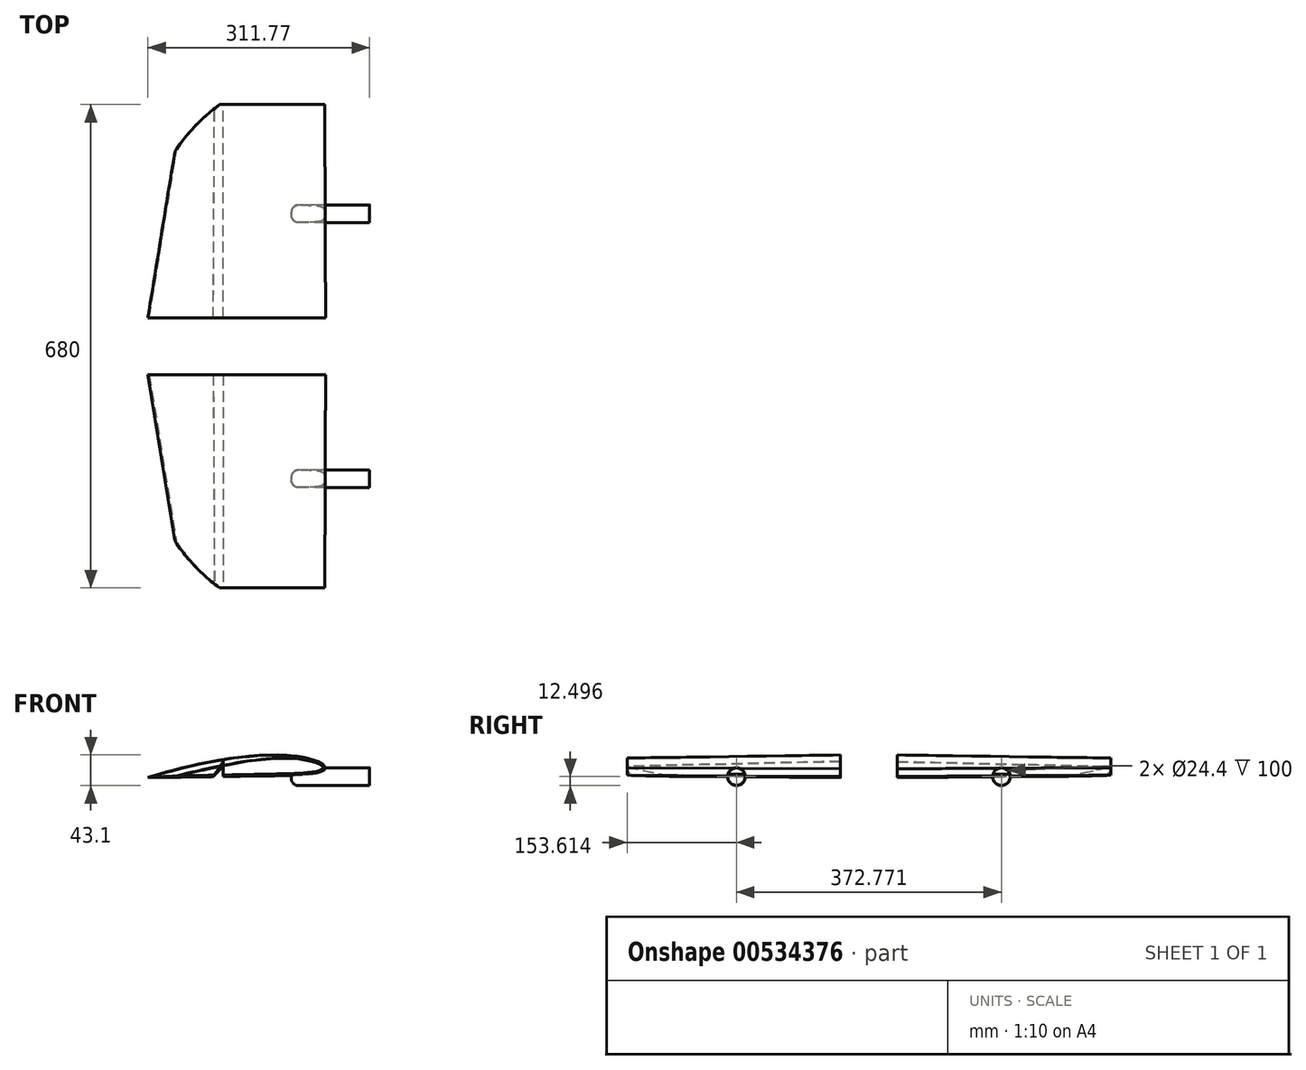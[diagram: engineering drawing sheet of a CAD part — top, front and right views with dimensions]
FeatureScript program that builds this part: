
annotation { "Feature Type Name" : "Feature", "Feature Type Description" : "" }
export const myFeature = defineFeature(function(context is Context, id is Id, definition is map)
    precondition{}
    {
        {
            var Q0;
            Q0=qCreatedBy(makeId("Front.planeOp"),FACE);
            var sketch = newSketch(context, id + "F0", { "sketchPlane" : qUnion([Q0])});
            skFitSpline(sketch, "E0.0.0", {"points": [v(128.23, 37.15) * mm, v(128.28, 37.44) * mm, v(128.28, 38.04) * mm, v(128.05, 38.94) * mm, v(127.62, 39.8) * mm, v(127.03, 40.64) * mm, v(126.33, 41.42) * mm, v(125.54, 42.16) * mm, v(124.7, 42.86) * mm, v(123.52, 43.74) * mm, v(121.98, 44.75) * mm, v(120.1, 45.83) * mm, v(118.53, 46.62) * mm, v(117.3, 47.2) * mm, v(116.38, 47.59) * mm, v(115.47, 47.96) * mm, v(114.57, 48.31) * mm, v(113.66, 48.64) * mm, v(112.75, 48.96) * mm, v(111.84, 49.27) * mm, v(110.6, 49.67) * mm, v(109, 50.17) * mm, v(107.06, 50.76) * mm, v(105.09, 51.33) * mm, v(103.1, 51.88) * mm, v(101.1, 52.4) * mm, v(99.12, 52.87) * mm, v(97.15, 53.31) * mm, v(95.18, 53.71) * mm, v(93.2, 54.08) * mm, v(91.23, 54.41) * mm, v(88.57, 54.83) * mm, v(85.22, 55.28) * mm, v(81.18, 55.73) * mm, v(77.14, 56.06) * mm, v(73.1, 56.3) * mm, v(69.07, 56.46) * mm, v(65.02, 56.57) * mm, v(59.62, 56.64) * mm, v(54.22, 56.62) * mm, v(48.82, 56.5) * mm, v(44.78, 56.38) * mm, v(40.73, 56.22) * mm, v(36.7, 56.02) * mm, v(32.65, 55.78) * mm, v(27.27, 55.4) * mm, v(20.55, 54.85) * mm, v(13.83, 54.19) * mm, v(8.47, 53.59) * mm, v(4.45, 53.1) * mm, v(0.43, 52.59) * mm, v(-4.92, 51.86) * mm, v(-11.6, 50.88) * mm, v(-18.25, 49.8) * mm, v(-23.57, 48.9) * mm, v(-27.55, 48.18) * mm, v(-31.53, 47.44) * mm, v(-36.82, 46.43) * mm, v(-43.4, 45.1) * mm, v(-49.97, 43.7) * mm, v(-55.24, 42.54) * mm, v(-59.19, 41.65) * mm, v(-63.13, 40.73) * mm, v(-67.06, 39.8) * mm, v(-70.98, 38.86) * mm, v(-74.25, 38.05) * mm, v(-76.87, 37.4) * mm, v(-79.49, 36.74) * mm, v(-84.07, 35.57) * mm, v(-88.66, 34.37) * mm, v(-92.57, 33.32) * mm, v(-94.53, 32.8) * mm, v(-96.48, 32.26) * mm, v(-98.44, 31.73) * mm, v(-100.42, 31.18) * mm, v(-102.4, 30.63) * mm, v(-104.36, 30.08) * mm, v(-106.3, 29.53) * mm, v(-108.25, 28.97) * mm, v(-110.2, 28.41) * mm, v(-112.13, 27.84) * mm, v(-114.7, 27.08) * mm, v(-117.91, 26.1) * mm, v(-120.48, 25.29) * mm, v(-121.77, 24.87) * mm]});
            skFitSpline(sketch, "E0.0.1", {"points": [v(-121.77, 24.87) * mm, v(-120.44, 24.86) * mm, v(-117.77, 24.85) * mm, v(-113.77, 24.85) * mm, v(-109.82, 24.88) * mm, v(-105.88, 24.93) * mm, v(-101.92, 24.98) * mm, v(-97.92, 25.04) * mm, v(-93.93, 25.1) * mm, v(-89.93, 25.16) * mm, v(-86.6, 25.21) * mm, v(-83.93, 25.25) * mm, v(-81.93, 25.28) * mm, v(-79.94, 25.31) * mm, v(-77.97, 25.34) * mm, v(-76.05, 25.37) * mm, v(-74.17, 25.4) * mm, v(-72.34, 25.43) * mm, v(-69.94, 25.46) * mm, v(-67.55, 25.5) * mm, v(-65.12, 25.54) * mm, v(-63.26, 25.56) * mm, v(-61.35, 25.6) * mm, v(-59.4, 25.62) * mm, v(-57.74, 25.64) * mm, v(-56.4, 25.66) * mm, v(-55.07, 25.68) * mm, v(-53.4, 25.7) * mm, v(-50.74, 25.74) * mm, v(-47.41, 25.8) * mm, v(-43.41, 25.85) * mm, v(-40.08, 25.9) * mm, v(-37.42, 25.94) * mm, v(-35.42, 25.97) * mm, v(-33.42, 26) * mm, v(-31.42, 26.02) * mm, v(-29.42, 26.05) * mm, v(-27.47, 26.08) * mm, v(-25.57, 26.1) * mm, v(-23.73, 26.14) * mm, v(-21.95, 26.16) * mm, v(-19.62, 26.2) * mm, v(-17.32, 26.23) * mm, v(-14.96, 26.27) * mm, v(-13.15, 26.3) * mm, v(-11.27, 26.32) * mm, v(-9.34, 26.35) * mm, v(-7.69, 26.37) * mm, v(-6.35, 26.39) * mm, v(-5.02, 26.4) * mm, v(-3.36, 26.43) * mm, v(-0.7, 26.47) * mm, v(2.64, 26.52) * mm, v(6.64, 26.58) * mm, v(11.97, 26.66) * mm, v(18.63, 26.75) * mm, v(26.63, 26.86) * mm, v(34.62, 26.98) * mm, v(42.62, 27.1) * mm, v(50.61, 27.2) * mm, v(57.27, 27.3) * mm, v(62.6, 27.39) * mm, v(66.6, 27.46) * mm, v(70.6, 27.53) * mm, v(74.59, 27.62) * mm, v(77.9, 27.7) * mm, v(80.57, 27.79) * mm, v(82.58, 27.86) * mm, v(84.58, 27.93) * mm, v(86.59, 28.01) * mm, v(88.58, 28.1) * mm, v(90.57, 28.18) * mm, v(92.55, 28.27) * mm, v(94.53, 28.37) * mm, v(96.52, 28.5) * mm, v(98.52, 28.63) * mm, v(100.54, 28.8) * mm, v(102.56, 28.98) * mm, v(104.59, 29.17) * mm, v(106.6, 29.37) * mm, v(108.57, 29.57) * mm, v(110.5, 29.75) * mm, v(112.4, 29.94) * mm, v(114.3, 30.16) * mm, v(115.92, 30.41) * mm, v(117.24, 30.67) * mm, v(118.58, 30.97) * mm, v(120.29, 31.43) * mm, v(122.33, 32.13) * mm, v(123.99, 32.86) * mm, v(125.23, 33.55) * mm, v(126.1, 34.13) * mm, v(126.88, 34.78) * mm, v(127.53, 35.5) * mm, v(128.01, 36.3) * mm, v(128.19, 36.86) * mm, v(128.23, 37.15) * mm]});
            skLineSegment(sketch, "E1", {"start": v(-15.83, 26.25) * mm, "end": v(-15.83, 46.77) * mm});
            skLineSegment(sketch, "E2", {"start": v(-15.83, 46.77) * mm, "end": v(-29.65, 26.05) * mm});
            skSolve(sketch);
        }
        {
            var Q0;
            Q0=qCreatedBy(makeId("Front.planeOp"),FACE);
            cPlane(context, id + "F1", {"entities" : qUnion([Q0]), "cplaneType" : CPlaneType.OFFSET, "offset" : 300 * mm, "width" : 150 * mm, "height" : 150 * mm});
        }
        {
            var Q0;
            Q0=qCreatedBy(id+"F1.planeOp",FACE);
            var sketch = newSketch(context, id + "F2", { "sketchPlane" : qUnion([Q0])});
            skFitSpline(sketch, "E3.0.0", {"points": [v(127.87, 35.85) * mm, v(127.9, 36.15) * mm, v(127.88, 36.74) * mm, v(127.6, 37.63) * mm, v(127.12, 38.48) * mm, v(126.5, 39.28) * mm, v(125.75, 40.03) * mm, v(124.93, 40.73) * mm, v(124.05, 41.38) * mm, v(122.83, 42.2) * mm, v(121.24, 43.13) * mm, v(119.3, 44.12) * mm, v(117.7, 44.83) * mm, v(116.43, 45.34) * mm, v(115.5, 45.69) * mm, v(114.57, 46.01) * mm, v(113.65, 46.32) * mm, v(112.73, 46.6) * mm, v(111.8, 46.88) * mm, v(110.87, 47.14) * mm, v(109.6, 47.48) * mm, v(108, 47.9) * mm, v(106.02, 48.39) * mm, v(104.02, 48.86) * mm, v(102, 49.3) * mm, v(99.99, 49.72) * mm, v(97.98, 50.1) * mm, v(95.99, 50.44) * mm, v(94, 50.74) * mm, v(92, 51) * mm, v(90, 51.24) * mm, v(87.33, 51.52) * mm, v(83.96, 51.8) * mm, v(79.9, 52.05) * mm, v(75.85, 52.18) * mm, v(71.8, 52.21) * mm, v(67.75, 52.17) * mm, v(63.7, 52.07) * mm, v(58.3, 51.87) * mm, v(52.9, 51.57) * mm, v(47.52, 51.2) * mm, v(43.48, 50.87) * mm, v(39.44, 50.5) * mm, v(35.41, 50.1) * mm, v(31.39, 49.65) * mm, v(26.02, 49) * mm, v(19.33, 48.11) * mm, v(12.66, 47.1) * mm, v(7.32, 46.24) * mm, v(3.33, 45.55) * mm, v(-0.66, 44.84) * mm, v(-5.97, 43.84) * mm, v(-12.6, 42.52) * mm, v(-19.2, 41.11) * mm, v(-24.46, 39.93) * mm, v(-28.41, 39.02) * mm, v(-32.35, 38.08) * mm, v(-37.59, 36.8) * mm, v(-44.1, 35.14) * mm, v(-50.6, 33.41) * mm, v(-55.8, 31.98) * mm, v(-59.7, 30.9) * mm, v(-63.6, 29.78) * mm, v(-67.48, 28.65) * mm, v(-71.35, 27.5) * mm, v(-74.58, 26.54) * mm, v(-77.17, 25.75) * mm, v(-79.75, 24.96) * mm, v(-84.27, 23.56) * mm, v(-88.8, 22.13) * mm, v(-92.66, 20.89) * mm, v(-94.58, 20.26) * mm, v(-96.5, 19.63) * mm, v(-98.45, 19) * mm, v(-100.4, 18.35) * mm, v(-102.34, 17.7) * mm, v(-104.27, 17.05) * mm, v(-106.2, 16.4) * mm, v(-108.11, 15.75) * mm, v(-110.03, 15.09) * mm, v(-111.93, 14.42) * mm, v(-114.46, 13.53) * mm, v(-117.62, 12.38) * mm, v(-120.15, 11.44) * mm, v(-121.42, 10.97) * mm]});
            skFitSpline(sketch, "E3.0.1", {"points": [v(-122.73, 26.21) * mm, v(-121.4, 26.2) * mm, v(-118.72, 26.2) * mm, v(-114.72, 26.23) * mm, v(-110.76, 26.28) * mm, v(-106.83, 26.34) * mm, v(-102.86, 26.42) * mm, v(-98.86, 26.5) * mm, v(-94.86, 26.58) * mm, v(-90.86, 26.66) * mm, v(-87.53, 26.72) * mm, v(-84.86, 26.78) * mm, v(-82.86, 26.82) * mm, v(-80.86, 26.86) * mm, v(-78.9, 26.9) * mm, v(-76.97, 26.94) * mm, v(-75.1, 26.98) * mm, v(-73.26, 27.01) * mm, v(-70.85, 27.06) * mm, v(-68.47, 27.1) * mm, v(-66.03, 27.16) * mm, v(-64.17, 27.2) * mm, v(-62.26, 27.23) * mm, v(-60.3, 27.27) * mm, v(-58.64, 27.3) * mm, v(-57.3, 27.33) * mm, v(-55.98, 27.35) * mm, v(-54.3, 27.38) * mm, v(-51.64, 27.44) * mm, v(-48.3, 27.5) * mm, v(-44.3, 27.58) * mm, v(-40.97, 27.64) * mm, v(-38.3, 27.7) * mm, v(-36.3, 27.73) * mm, v(-34.3, 27.77) * mm, v(-32.3, 27.81) * mm, v(-30.3, 27.85) * mm, v(-28.35, 27.89) * mm, v(-26.45, 27.93) * mm, v(-24.6, 27.96) * mm, v(-22.82, 28) * mm, v(-20.49, 28.04) * mm, v(-18.19, 28.09) * mm, v(-15.83, 28.13) * mm, v(-14.01, 28.17) * mm, v(-12.14, 28.2) * mm, v(-10.2, 28.24) * mm, v(-8.55, 28.28) * mm, v(-7.22, 28.3) * mm, v(-5.88, 28.33) * mm, v(-4.22, 28.36) * mm, v(-1.55, 28.41) * mm, v(1.78, 28.48) * mm, v(5.79, 28.55) * mm, v(11.12, 28.66) * mm, v(17.79, 28.79) * mm, v(25.79, 28.94) * mm, v(33.79, 29.1) * mm, v(41.8, 29.25) * mm, v(49.8, 29.4) * mm, v(56.46, 29.53) * mm, v(61.8, 29.64) * mm, v(65.8, 29.73) * mm, v(69.8, 29.83) * mm, v(73.79, 29.93) * mm, v(77.1, 30.03) * mm, v(79.78, 30.13) * mm, v(81.78, 30.21) * mm, v(83.8, 30.3) * mm, v(85.8, 30.39) * mm, v(87.8, 30.48) * mm, v(89.79, 30.58) * mm, v(91.77, 30.68) * mm, v(93.75, 30.79) * mm, v(95.74, 30.91) * mm, v(97.74, 31.06) * mm, v(99.76, 31.24) * mm, v(101.78, 31.43) * mm, v(103.8, 31.64) * mm, v(105.81, 31.85) * mm, v(107.79, 32.05) * mm, v(109.72, 32.25) * mm, v(111.63, 32.44) * mm, v(113.53, 32.68) * mm, v(115.15, 32.94) * mm, v(116.47, 33.2) * mm, v(117.8, 33.5) * mm, v(119.51, 33.97) * mm, v(121.56, 34.69) * mm, v(123.2, 35.43) * mm, v(124.45, 36.12) * mm, v(125.31, 36.7) * mm, v(126.1, 37.36) * mm, v(126.74, 38.08) * mm, v(127.22, 38.88) * mm, v(127.39, 39.45) * mm, v(127.43, 39.74) * mm]});
            skLineSegment(sketch, "E4", {"start": v(-15.82, 28.13) * mm, "end": v(-15.82, 40.03) * mm});
            skLineSegment(sketch, "E5", {"start": v(-15.82, 40.03) * mm, "end": v(-28.06, 27.9) * mm});
            skSolve(sketch);
        }
        {
            var Q0;
            Q0=makeQuery(id+"F0.imprint","IMPRINT",FACE,{"disambiguationData":[TD([[makeQuery(id+"F0.imprint","IMPRINT",EDGE,{"derivedFrom":sQuery(id+"F0.wireOp",EDGE,"E0.0.0")}),1.0]])]});
            var Q1;
            Q1=makeQuery(id+"F2.imprint","IMPRINT",FACE,{"disambiguationData":[TD([[makeQuery(id+"F2.imprint","IMPRINT",EDGE,{"derivedFrom":sQuery(id+"F2.wireOp",EDGE,"E3.0.0")}),1.0]])]});
            loft(context, id + "F3", {"sheetProfilesArray" : [{ "sheetProfileEntities" : qUnion([Q0]) }, { "sheetProfileEntities" : qUnion([Q1]) }]});
        }
        {
            var Q0;
            Q0=qCreatedBy(makeId("Front.planeOp"),FACE);
            cPlane(context, id + "F4", {"entities" : qUnion([Q0]), "cplaneType" : CPlaneType.OFFSET, "offset" : 40 * mm, "oppositeDirection" : true, "width" : 150 * mm, "height" : 150 * mm});
        }
        {
            var Q0;
            Q0=makeQuery(id+"F3.opLoft","SWEPT_BODY",BODY,{"disambiguationData":[OSD([makeQuery(id+"F0.imprint","IMPRINT",FACE,{"disambiguationData":[TD([[makeQuery(id+"F0.imprint","IMPRINT",EDGE,{"derivedFrom":sQuery(id+"F0.wireOp",EDGE,"E0.0.0")}),1.0]])]}),makeQuery(id+"F2.imprint","IMPRINT",FACE,{"disambiguationData":[TD([[makeQuery(id+"F2.imprint","IMPRINT",EDGE,{"derivedFrom":sQuery(id+"F2.wireOp",EDGE,"E3.0.0")}),1.0]])]})])]});
            var Q1;
            Q1=qCreatedBy(id+"F4.planeOp",FACE);
            mirror(context, id + "F5", {"entities" : qUnion([Q0]), "mirrorPlane" : qUnion([Q1])});
        }
        {
            var Q0;
            Q0=qCreatedBy(makeId("Right.planeOp"),FACE);
            cPlane(context, id + "F6", {"entities" : qUnion([Q0]), "cplaneType" : CPlaneType.OFFSET, "offset" : 80 * mm, "width" : 150 * mm, "height" : 150 * mm});
        }
        {
            var Q0;
            Q0=qCreatedBy(id+"F6.planeOp",FACE);
            var sketch = newSketch(context, id + "F7", { "sketchPlane" : qUnion([Q0])});
            skCircle(sketch, "E6", {"center": v(-146.39, 26.05) * mm, "radius": 12.5 * mm});
            skCircle(sketch, "E7.MirrorC", {"center": v(226.39, 26.05) * mm, "radius": 12.5 * mm});
            skSolve(sketch);
        }
        {
            var Q0;
            Q0=qSketchRegion(id+"F7",true);
            extrude(context, id + "F8", {"entities" : qUnion([Q0]), "operationType" : NewBodyOperationType.ADD, "depth" : 110 * mm, "offsetDistance" : 25 * mm});
        }
        {
            var Q0;
            Q0=makeQuery(id+"F8.opExtrude","CAP_EDGE",EDGE,{"disambiguationData":[OSD([sQuery(id+"F7.wireOp",EDGE,"E6")])],"isStart":true});
            var Q1;
            Q1=makeQuery(id+"F8.opExtrude","CAP_EDGE",EDGE,{"disambiguationData":[OSD([sQuery(id+"F7.wireOp",EDGE,"E7.MirrorC")])],"isStart":true});
            fillet(context, id + "F9", {"entities" : qUnion([Q0, Q1]), "radius" : 10 * mm, "tangentPropagation" : true, "allowEdgeOverflow" : false});
        }
        {
            var Q0;
            {var subQ2=sQuery(id+"F2.wireOp",EDGE,"E3.0.0");Q0=makeQuery(id+"F3.opLoft","CAP_FACE",FACE,{"disambiguationData":[OSD([makeQuery(id+"F2.imprint","IMPRINT",FACE,{"disambiguationData":[TD([[makeQuery(id+"F2.imprint","IMPRINT",EDGE,{"derivedFrom":subQ2}),1.0]])]})])],"isStart":true});}
            var Q1;
            {var subQ2=sQuery(id+"F2.wireOp",EDGE,"E3.0.0");Q1=makeQuery(id+"F5.opPattern","COPY",FACE,{"derivedFrom":makeQuery(id+"F3.opLoft","CAP_FACE",FACE,{"disambiguationData":[OSD([makeQuery(id+"F2.imprint","IMPRINT",FACE,{"disambiguationData":[TD([[makeQuery(id+"F2.imprint","IMPRINT",EDGE,{"derivedFrom":subQ2}),1.0]])]})])],"isStart":true}),"instanceName":"1"});}
            var Q2;
            Q2=makeQuery(id+"F8.opExtrude","CAP_FACE",FACE,{"disambiguationData":[OSD([sQuery(id+"F7.wireOp",EDGE,"E7.MirrorC")])],"isStart":false});
            var Q3;
            Q3=makeQuery(id+"F8.opExtrude","CAP_FACE",FACE,{"disambiguationData":[OSD([sQuery(id+"F7.wireOp",EDGE,"E6")])],"isStart":false});
            shell(context, id + "F10", {"entities" : qUnion([Q0, Q1, Q2, Q3]), "thickness" : .3 * mm});
        }
        {
            var Q0;
            Q0=qCreatedBy(makeId("Top.planeOp"),FACE);
            var sketch = newSketch(context, id + "F11", { "sketchPlane" : qUnion([Q0])});
            skLineSegment(sketch, "E8", {"start": v(-86.82, 309.23) * mm, "end": v(-73.01, 383.16) * mm});
            skLineSegment(sketch, "E9", {"start": v(-73.01, 383.16) * mm, "end": v(-16.27, 383.16) * mm});
            skArc(sketch, "E10.MirrorCS", {"start": v(-16.27, -303.16) * mm, "mid": v(-55.27, -269.75) * mm, "end": v(-86.82, -229.23) * mm});
            skLineSegment(sketch, "E11.MirrorCS", {"start": v(-86.82, -229.23) * mm, "end": v(-73.01, -303.16) * mm});
            skLineSegment(sketch, "E12.MirrorCS", {"start": v(-73.01, -303.16) * mm, "end": v(-16.27, -303.16) * mm});
            skArc(sketch, "E13.MirrorCS", {"start": v(-16.27, 383.16) * mm, "mid": v(-55.27, 349.75) * mm, "end": v(-86.82, 309.23) * mm});
            skSolve(sketch);
        }
        {
            var Q0;
            Q0=qSketchRegion(id+"F11",true);
            extrude(context, id + "F12", {"entities" : qUnion([Q0]), "operationType" : NewBodyOperationType.REMOVE, "depth" : 70 * mm, "offsetDistance" : 25 * mm});
        }
    });
